# Revit family: WAC_A3-Lintel-Brick-Double-Cant-(UK)
name_source: partatom
category: Generic Models
revit_build: Autodesk Revit 2016 (Build: 20150220_1215(x64)
units: mm (PartAtom-declared; Revit-internal decimal feet)

## family parameters
Always vertical = Yes
Can host rebar = No
Cut with Voids When Loaded = No
Host = Wall
Part Type = Undefined
Room Calculation Point = No
Round Connector Dimension = Use Diameter
Shared = No

## types (2) — shared parameters
Chamfer Dist = 25 mm  [stored 0.082021 ft]
Lintol Bearing = 150 mm
Lintol Offset from Ext = 25 mm  [stored 0.082021 ft]
Lintol Width = 125 mm  [stored 0.410105 ft]
Material Lintol = Masonry - Brick Soldier Course

## per-type parameters (varying)
| type | Lintol Depth |
| 125 x 215mm Deep | 215 mm  [stored 0.705381 ft] |
| 125 x 150mm Deep | 150 mm |

note: [stored X ft] marks values corroborated as IEEE doubles in the binary element streams (Revit-internal decimal feet)

## geometry (parser evidence)
native form markers: Sweep x2
no freeform markers — native parametric forms only
